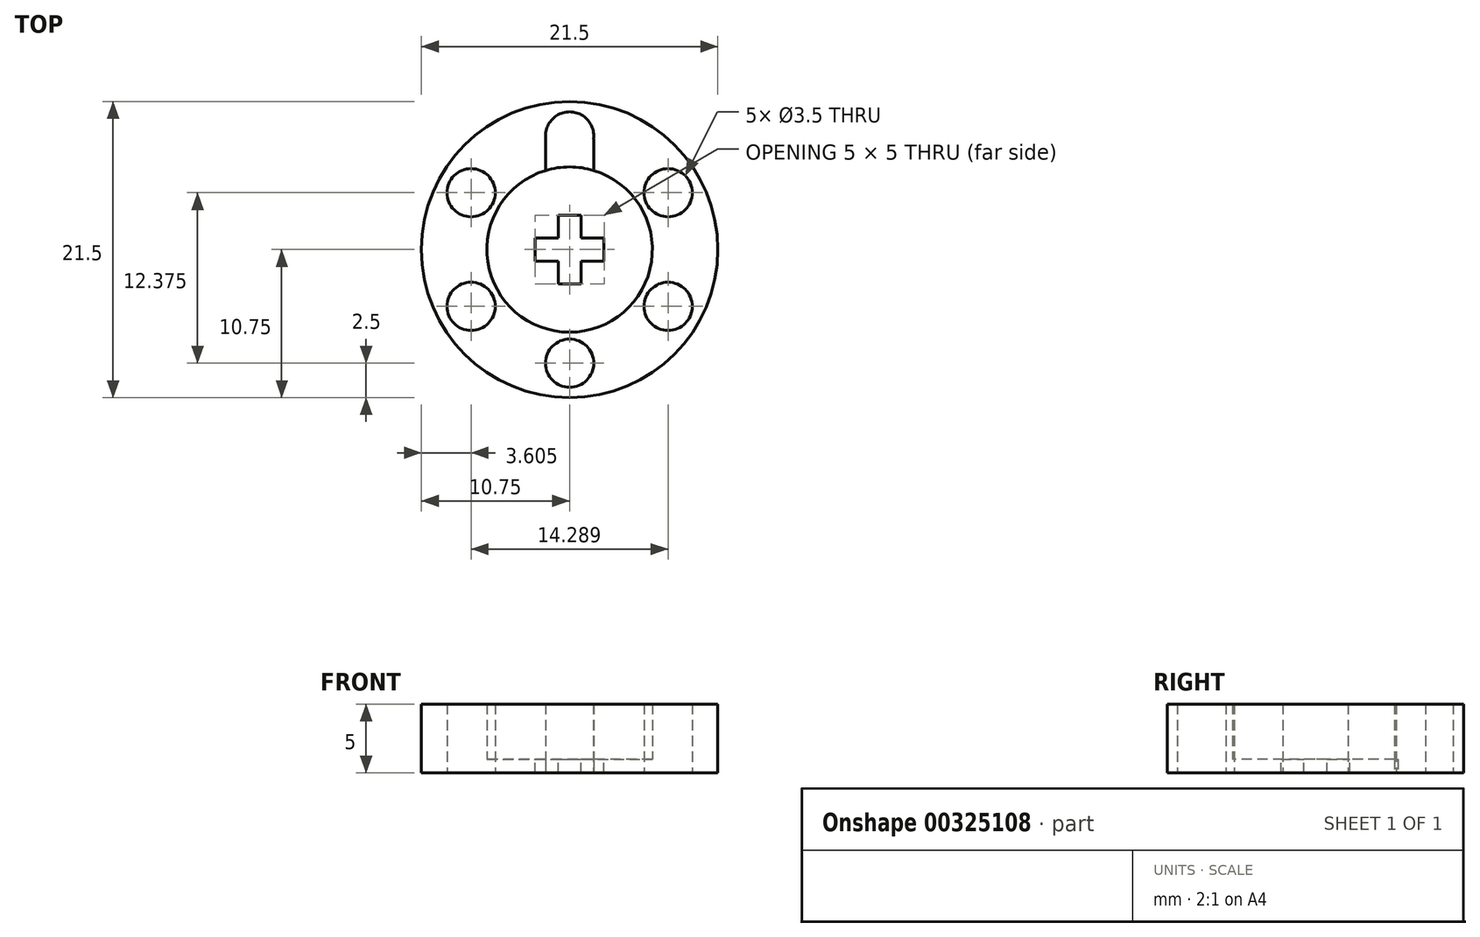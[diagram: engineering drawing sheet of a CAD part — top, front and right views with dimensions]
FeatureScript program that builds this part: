
annotation { "Feature Type Name" : "Feature", "Feature Type Description" : "" }
export const myFeature = defineFeature(function(context is Context, id is Id, definition is map)
    precondition{}
    {
        {
            var Q0;
            Q0=qCreatedBy(makeId("Top.planeOp"),FACE);
            var sketch = newSketch(context, id + "F0", { "sketchPlane" : qUnion([Q0])});
            skLineSegment(sketch, "E0", {"start": v(-0.83, 2.5) * mm, "end": v(0.83, 2.5) * mm});
            skLineSegment(sketch, "E1", {"start": v(0.83, -2.5) * mm, "end": v(-0.83, -2.5) * mm});
            skLineSegment(sketch, "E2.left", {"start": v(-2.5, 0.83) * mm, "end": v(-2.5, -0.83) * mm});
            skLineSegment(sketch, "E2.right", {"start": v(2.5, 0.83) * mm, "end": v(2.5, -0.83) * mm});
            skPoint(sketch, "E3", {"position": v(-0.83, 0.83) * mm});
            skPoint(sketch, "E4", {"position": v(0.83, 0.83) * mm});
            skPoint(sketch, "E5", {"position": v(0.83, -0.83) * mm});
            skPoint(sketch, "E6", {"position": v(-0.83, -0.83) * mm});
            skLineSegment(sketch, "E7", {"start": v(-0.83, -2.5) * mm, "end": v(-0.83, -0.83) * mm});
            skLineSegment(sketch, "E8", {"start": v(-0.83, -0.83) * mm, "end": v(-0.83, 0.83) * mm});
            skLineSegment(sketch, "E9", {"start": v(-0.83, 0.83) * mm, "end": v(-0.83, 2.5) * mm});
            skLineSegment(sketch, "E10", {"start": v(-2.5, -0.83) * mm, "end": v(-0.83, -0.83) * mm});
            skLineSegment(sketch, "E11", {"start": v(0.83, -0.83) * mm, "end": v(2.5, -0.83) * mm});
            skLineSegment(sketch, "E12", {"start": v(-0.83, -0.83) * mm, "end": v(0.83, -0.83) * mm});
            skLineSegment(sketch, "E13", {"start": v(-2.5, 0.83) * mm, "end": v(-0.83, 0.83) * mm});
            skLineSegment(sketch, "E14", {"start": v(-0.83, 0.83) * mm, "end": v(0.83, 0.83) * mm});
            skLineSegment(sketch, "E15", {"start": v(2.5, 0.83) * mm, "end": v(0.83, 0.83) * mm});
            skLineSegment(sketch, "E16", {"start": v(0.83, 2.5) * mm, "end": v(0.83, 0.83) * mm});
            skLineSegment(sketch, "E17", {"start": v(0.83, -0.83) * mm, "end": v(0.83, 0.83) * mm});
            skLineSegment(sketch, "E18", {"start": v(0.83, -2.5) * mm, "end": v(0.83, -0.83) * mm});
            skPoint(sketch, "E19", {"position": v(0, 0) * mm});
            skLineSegment(sketch, "E20", {"start": v(-0.83, -0.83) * mm, "end": v(0.83, 0.83) * mm, "construction": true});
            skLineSegment(sketch, "E21", {"start": v(-0.83, 0.83) * mm, "end": v(0.83, -0.83) * mm, "construction": true});
            skSolve(sketch);
        }
        {
            var Q0;
            Q0=qCreatedBy(makeId("Top.planeOp"),FACE);
            var sketch = newSketch(context, id + "F1", { "sketchPlane" : qUnion([Q0])});
            skCircle(sketch, "E22", {"center": v(0, 0) * mm, "radius": 6 * mm});
            skLineSegment(sketch, "E23", {"start": v(-1.75, 5.74) * mm, "end": v(-1.75, 8) * mm});
            skLineSegment(sketch, "E24", {"start": v(-1.75, 8) * mm, "end": v(1.75, 8) * mm});
            skLineSegment(sketch, "E25", {"start": v(1.75, 8) * mm, "end": v(1.75, 5.74) * mm});
            skPoint(sketch, "E26", {"position": v(0, 8) * mm});
            skCircle(sketch, "E27", {"center": v(0, 0) * mm, "radius": 10.75 * mm});
            skCircle(sketch, "E28", {"center": v(0, 0) * mm, "radius": 10 * mm});
            skCircle(sketch, "E29", {"center": v(0, -8.25) * mm, "radius": 1.75 * mm});
            skPoint(sketch, "E30", {"position": v(0, -10) * mm});
            skCircle(sketch, "E31.1.0", {"center": v(7.14, -4.13) * mm, "radius": 1.75 * mm});
            skCircle(sketch, "E31.2.0", {"center": v(7.14, 4.12) * mm, "radius": 1.75 * mm});
            skCircle(sketch, "E31.3.0", {"center": v(0, 8.25) * mm, "radius": 1.75 * mm});
            skCircle(sketch, "E31.4.0", {"center": v(-7.14, 4.13) * mm, "radius": 1.75 * mm});
            skCircle(sketch, "E31.5.0", {"center": v(-7.14, -4.13) * mm, "radius": 1.75 * mm});
            skSolve(sketch);
        }
        {
            var Q0;
            {var subQ14=sQuery(id+"F1.wireOp",EDGE,"E23");Q0=makeQuery(id+"F1.imprint","IMPRINT",FACE,{"disambiguationData":[TD([[makeQuery(id+"F1.imprint","IMPRINT",EDGE,{"derivedFrom":subQ14}),1.0]])]});}
            var Q1;
            Q1=makeQuery(id+"F1.imprint","IMPRINT",FACE,{"disambiguationData":[TD([[makeQuery(id+"F1.imprint","IMPRINT",EDGE,{"derivedFrom":sQuery(id+"F1.wireOp",EDGE,"E27")}),1.0]])]});
            extrude(context, id + "F2", {"entities" : qUnion([Q0, Q1]), "depth" : 5 * mm});
        }
        {
            var Q0;
            {var subQ0=sQuery(id+"F1.wireOp",EDGE,"E22");var subQ1=makeQuery(id+"F1.imprint","INTERSECT",VERTEX,{"derivedFrom":[subQ0,sQuery(id+"F1.wireOp",EDGE,"E23")]});Q0=makeQuery(id+"F1.imprint","IMPRINT",FACE,{"disambiguationData":[TD([[makeQuery(id+"F1.imprint","IMPRINT",EDGE,{"disambiguationData":[TD([[subQ1,1.0]])],"derivedFrom":subQ0}),1.0]])]});}
            extrude(context, id + "F3", {"entities" : qUnion([Q0]), "operationType" : NewBodyOperationType.ADD, "depth" : 1 * mm});
        }
        {
            var Q0;
            Q0 = qSketchRegion(id + "F0", true);
            extrude(context, id + "F4", {"entities" : qUnion([Q0]), "operationType" : NewBodyOperationType.REMOVE, "endBound" : BoundingType.SYMMETRIC, "oppositeDirection" : true, "depth" : 25 * mm});
        }
    });
